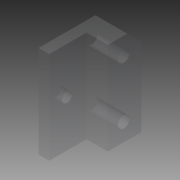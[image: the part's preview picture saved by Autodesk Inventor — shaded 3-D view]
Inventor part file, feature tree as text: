
AUTODESK INVENTOR PART (.ipt)
format: ipt  version: 2015 (Build 190159000, 159)  size: 103,936 bytes
history: native  units: mm
features: hole x3, other x2, extrude x2, sketch x2, chamfer x1
ambient origin geometry x8: Origin, YZ Plane, XZ Plane, XY Plane, X Axis, Y Axis, Z Axis, Center Point
bodies: Body1 (feature_tree)
feature tree (10):
  other  "솔리드1"
  extrude  "돌출1"  Depth=6.0mm
  extrude  "돌출2"  Depth=26.0mm
  hole  "구멍1"  [1 undecoded]
  hole  "구멍2"  [1 undecoded]
  hole  "구멍3"  [1 undecoded]
  other  "두껍게 하기1"
  chamfer  "모따기1"  Distance=5.0mm
  sketch  "스케치1"
  sketch  "스케치2"
note: 3 required parameter values undecoded (feature->parameter linkage not recoverable at this tier; creation-order binding heuristic only, values carry confidence <= 0.55)
